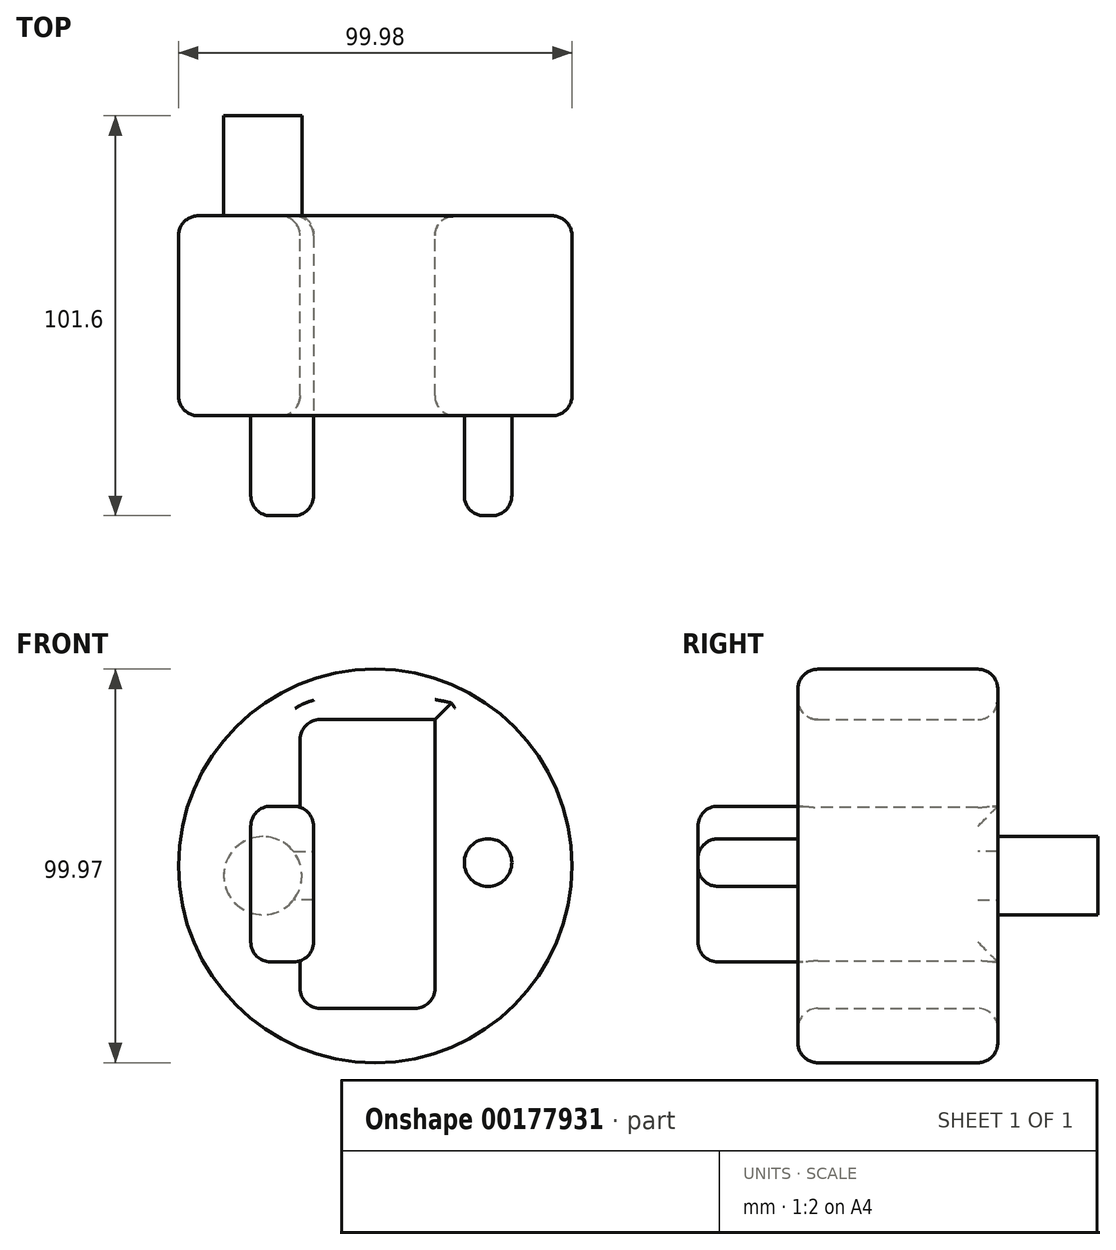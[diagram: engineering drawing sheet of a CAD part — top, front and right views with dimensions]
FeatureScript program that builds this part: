
annotation { "Feature Type Name" : "Feature", "Feature Type Description" : "" }
export const myFeature = defineFeature(function(context is Context, id is Id, definition is map)
    precondition{}
    {
        {
            var Q0;
            Q0=qCreatedBy(makeId("Front.planeOp"),FACE);
            var sketch = newSketch(context, id + "F0", { "sketchPlane" : qUnion([Q0])});
            skCircle(sketch, "E0", {"center": v(-73.85, 46.5) * mm, "radius": 49.99 * mm});
            skLineSegment(sketch, "E1", {"start": v(-73.85, 46.5) * mm, "end": v(-73.85, 87.96) * mm, "construction": true});
            skLineSegment(sketch, "E2.bottom", {"start": v(-92.92, 83.68) * mm, "end": v(-58.68, 83.68) * mm});
            skLineSegment(sketch, "E2.top", {"start": v(-92.92, 10.3) * mm, "end": v(-58.68, 10.3) * mm});
            skLineSegment(sketch, "E2.left", {"start": v(-92.92, 83.68) * mm, "end": v(-92.92, 10.3) * mm});
            skLineSegment(sketch, "E2.right", {"start": v(-58.68, 83.68) * mm, "end": v(-58.68, 10.3) * mm});
            skSolve(sketch);
        }
        {
            var Q0;
            Q0 = qSketchRegion(id + "F0", true);
            extrude(context, id + "F1", {"entities" : qUnion([Q0]), "depth" : 50.8 * mm});
        }
        {
            var Q0;
            Q0=makeQuery(id+"F1.opExtrude","CAP_FACE",FACE,{"disambiguationData":[OSD([sQuery(id+"F0.wireOp",EDGE,"E0"),sQuery(id+"F0.wireOp",EDGE,"E2.bottom"),sQuery(id+"F0.wireOp",EDGE,"E2.top"),sQuery(id+"F0.wireOp",EDGE,"E2.left"),sQuery(id+"F0.wireOp",EDGE,"E2.right")])],"isStart":false});
            var Q1;
            Q1=makeQuery(id+"F1.opExtrude","SWEPT_FACE",FACE,{"disambiguationData":[OSD([sQuery(id+"F0.wireOp",EDGE,"E2.left")])]});
            var Q2;
            Q2=makeQuery(id+"F1.opExtrude","SWEPT_FACE",FACE,{"disambiguationData":[OSD([sQuery(id+"F0.wireOp",EDGE,"E2.top")])]});
            var Q3;
            Q3=makeQuery(id+"F1.opExtrude","CAP_FACE",FACE,{"disambiguationData":[OSD([sQuery(id+"F0.wireOp",EDGE,"E0"),sQuery(id+"F0.wireOp",EDGE,"E2.bottom"),sQuery(id+"F0.wireOp",EDGE,"E2.top"),sQuery(id+"F0.wireOp",EDGE,"E2.left"),sQuery(id+"F0.wireOp",EDGE,"E2.right")])],"isStart":true});
            fillet(context, id + "F2", {"entities" : qUnion([Q0, Q1, Q2, Q3]), "radius" : 5.08 * mm, "tangentPropagation" : true, "allowEdgeOverflow" : false});
        }
        {
            var Q0;
            Q0=makeQuery(id+"F2.opFillet","SPLIT",FACE,{"disambiguationData":[OD(1.0)],"derivedFrom":makeQuery(id+"F1.opExtrude","CAP_FACE",FACE,{"disambiguationData":[OSD([sQuery(id+"F0.wireOp",EDGE,"E0"),sQuery(id+"F0.wireOp",EDGE,"E2.bottom"),sQuery(id+"F0.wireOp",EDGE,"E2.top"),sQuery(id+"F0.wireOp",EDGE,"E2.left"),sQuery(id+"F0.wireOp",EDGE,"E2.right")])],"isStart":false})});
            var sketch = newSketch(context, id + "F3", { "sketchPlane" : qUnion([Q0])});
            skCircle(sketch, "E3", {"center": v(-45.18, 47.35) * mm, "radius": 6.04 * mm});
            skLineSegment(sketch, "E4.bottom", {"start": v(-89.5, 22.08) * mm, "end": v(-105.45, 22.08) * mm});
            skLineSegment(sketch, "E4.top", {"start": v(-89.5, 61.65) * mm, "end": v(-105.45, 61.65) * mm});
            skLineSegment(sketch, "E4.left", {"start": v(-89.5, 22.08) * mm, "end": v(-89.5, 61.65) * mm});
            skLineSegment(sketch, "E4.right", {"start": v(-105.45, 22.08) * mm, "end": v(-105.45, 61.65) * mm});
            skSolve(sketch);
        }
        {
            var Q0;
            Q0 = qSketchRegion(id + "F3", true);
            var Q1;
            Q1=sQuery(id+"F3.wireOp",EDGE,"E3");
            var Q2;
            Q2=sQuery(id+"F3.wireOp",EDGE,"E4.right");
            extrude(context, id + "F4", {"entities" : qUnion([Q0]), "operationType" : NewBodyOperationType.ADD, "surfaceEntities" : qUnion([Q1, Q2]), "oppositeDirection" : true, "depth" : 50.8 * mm, "hasSecondDirection" : true, "secondDirectionOppositeDirection" : false, "secondDirectionDepth" : 25.4 * mm});
        }
        {
            var Q0;
            Q0=makeQuery(id+"F4.boolean.opBoolean","MERGE",FACE,{"derivedFrom":[makeQuery(id+"F2.opFillet","SPLIT",FACE,{"disambiguationData":[OD(0.0)],"derivedFrom":makeQuery(id+"F1.opExtrude","CAP_FACE",FACE,{"disambiguationData":[OSD([sQuery(id+"F0.wireOp",EDGE,"E0"),sQuery(id+"F0.wireOp",EDGE,"E2.bottom"),sQuery(id+"F0.wireOp",EDGE,"E2.top"),sQuery(id+"F0.wireOp",EDGE,"E2.left"),sQuery(id+"F0.wireOp",EDGE,"E2.right")])],"isStart":true})}),makeQuery(id+"F4.opExtrude","CAP_FACE",FACE,{"disambiguationData":[OSD([sQuery(id+"F3.wireOp",EDGE,"E4.bottom"),sQuery(id+"F3.wireOp",EDGE,"E4.top"),sQuery(id+"F3.wireOp",EDGE,"E4.left"),sQuery(id+"F3.wireOp",EDGE,"E4.right")])],"isStart":false})]});
            var sketch = newSketch(context, id + "F5", { "sketchPlane" : qUnion([Q0])});
            skCircle(sketch, "E5", {"center": v(102.39, 44.01) * mm, "radius": 9.92 * mm});
            skSolve(sketch);
        }
        {
            var Q0;
            Q0 = qSketchRegion(id + "F5", true);
            extrude(context, id + "F6", {"entities" : qUnion([Q0]), "operationType" : NewBodyOperationType.ADD, "depth" : 25.4 * mm});
        }
        {
            var Q0;
            Q0=makeQuery(id+"F4.boolean.opBoolean","MERGE",FACE,{"derivedFrom":[makeQuery(id+"F2.opFillet","SPLIT",FACE,{"disambiguationData":[OD(0.0)],"derivedFrom":makeQuery(id+"F1.opExtrude","CAP_FACE",FACE,{"disambiguationData":[OSD([sQuery(id+"F0.wireOp",EDGE,"E0"),sQuery(id+"F0.wireOp",EDGE,"E2.bottom"),sQuery(id+"F0.wireOp",EDGE,"E2.top"),sQuery(id+"F0.wireOp",EDGE,"E2.left"),sQuery(id+"F0.wireOp",EDGE,"E2.right")])],"isStart":true})}),makeQuery(id+"F4.opExtrude","CAP_FACE",FACE,{"disambiguationData":[OSD([sQuery(id+"F3.wireOp",EDGE,"E4.bottom"),sQuery(id+"F3.wireOp",EDGE,"E4.top"),sQuery(id+"F3.wireOp",EDGE,"E4.left"),sQuery(id+"F3.wireOp",EDGE,"E4.right")])],"isStart":false})]});
            var sketch = newSketch(context, id + "F7", { "sketchPlane" : qUnion([Q0])});
            skText(sketch, "E6", { "text": "A", "fontName": "OpenSans-Regular.ttf"});
            const initialGuessF7  = {"E6": [0.03686, 0.02514, 1, 0, 0.01728]};
            skSetInitialGuess(sketch, initialGuessF7);
            skSolve(sketch);
        }
        {
            var Q0;
            Q0 = qBodyType(qCreatedBy(id + "F7" ,EDGE), BodyType.WIRE);
            extrude(context, id + "F8", {"bodyType" : ToolBodyType.SURFACE, "surfaceEntities" : qUnion([Q0]), "oppositeDirection" : true, "depth" : 50.2 * mm});
        }
        {
            var Q0;
            Q0=makeQuery(id+"F4.opExtrude","SWEPT_EDGE",EDGE,{"disambiguationData":[OSD([sQuery(id+"F3.wireOp",EDGE,"E4.bottom"),sQuery(id+"F3.wireOp",EDGE,"E4.left")])]});
            var Q1;
            Q1=makeQuery(id+"F4.opExtrude","SWEPT_FACE",FACE,{"disambiguationData":[OSD([sQuery(id+"F3.wireOp",EDGE,"E4.left")])]});
            var Q2;
            Q2=makeQuery(id+"F4.opExtrude","CAP_EDGE",EDGE,{"disambiguationData":[OSD([sQuery(id+"F3.wireOp",EDGE,"E3")])],"isStart":true});
            var Q3;
            Q3=makeQuery(id+"F4.opExtrude","CAP_EDGE",EDGE,{"disambiguationData":[OSD([sQuery(id+"F3.wireOp",EDGE,"E4.right")])],"isStart":true});
            var Q4;
            Q4=makeQuery(id+"F4.opExtrude","SWEPT_EDGE",EDGE,{"disambiguationData":[OSD([sQuery(id+"F3.wireOp",EDGE,"E4.top"),sQuery(id+"F3.wireOp",EDGE,"E4.right")])]});
            var Q5;
            Q5=makeQuery(id+"F4.opExtrude","SWEPT_EDGE",EDGE,{"disambiguationData":[OSD([sQuery(id+"F3.wireOp",EDGE,"E4.bottom"),sQuery(id+"F3.wireOp",EDGE,"E4.right")])]});
            var Q6;
            Q6=makeQuery(id+"F4.opExtrude","CAP_EDGE",EDGE,{"disambiguationData":[OSD([sQuery(id+"F3.wireOp",EDGE,"E4.top")])],"isStart":true});
            var Q7;
            Q7=makeQuery(id+"F4.opExtrude","CAP_EDGE",EDGE,{"disambiguationData":[OSD([sQuery(id+"F3.wireOp",EDGE,"E4.bottom")])],"isStart":true});
            fillet(context, id + "F9", {"entities" : qUnion([Q0, Q1, Q2, Q3, Q4, Q5, Q6, Q7]), "radius" : 5.08 * mm, "tangentPropagation" : true, "allowEdgeOverflow" : false});
        }
    });
